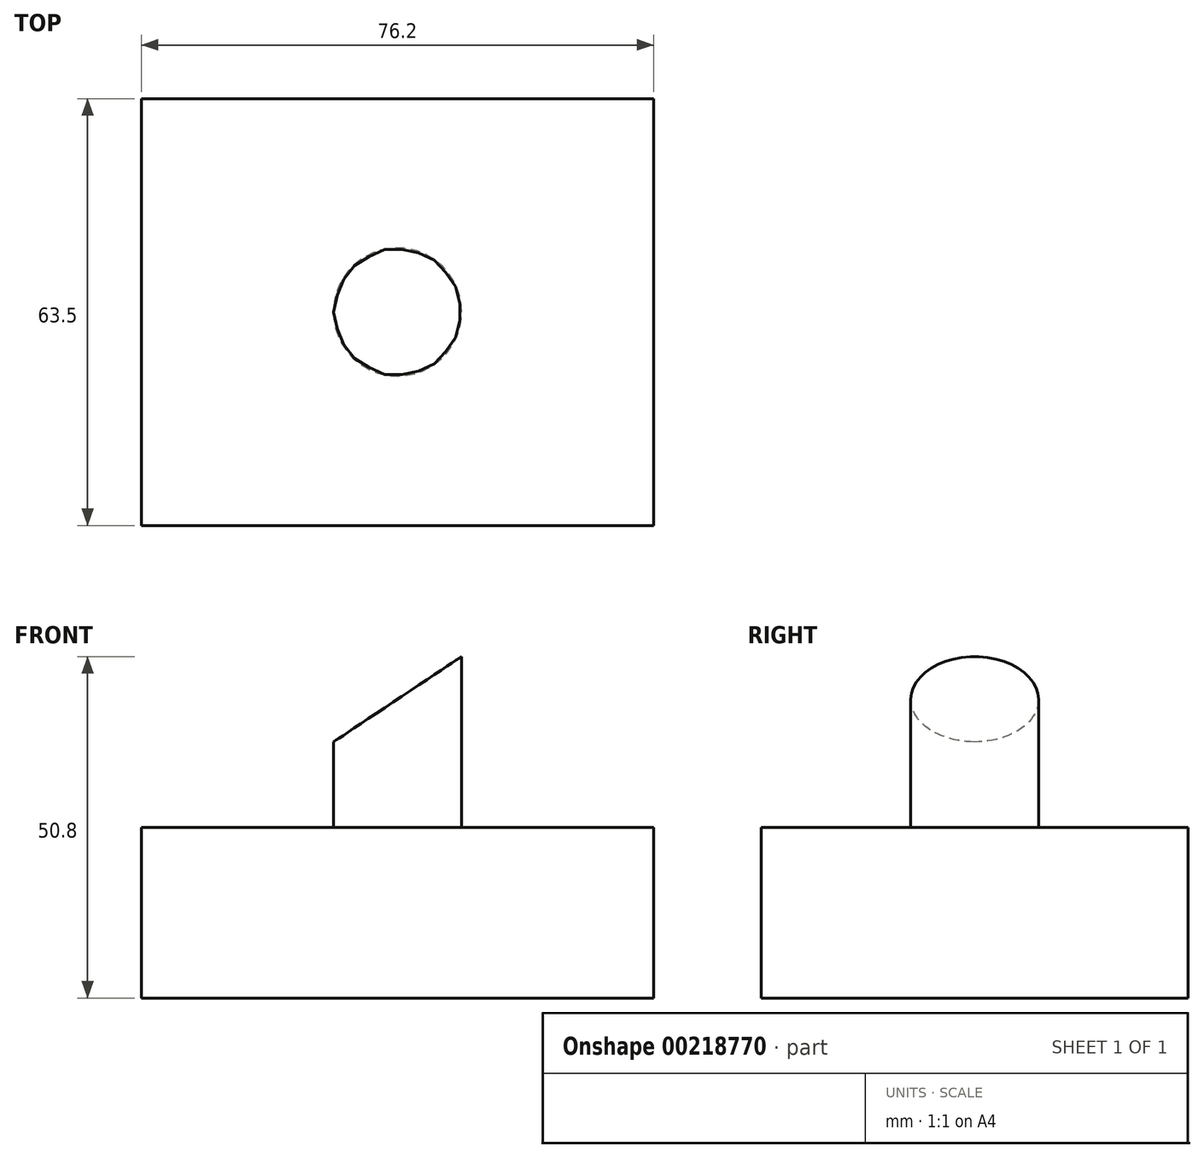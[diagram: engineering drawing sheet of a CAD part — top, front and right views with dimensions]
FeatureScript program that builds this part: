
annotation { "Feature Type Name" : "Feature", "Feature Type Description" : "" }
export const myFeature = defineFeature(function(context is Context, id is Id, definition is map)
    precondition{}
    {
        {
            var Q0;
            Q0=qCreatedBy(makeId("Top.planeOp"),FACE);
            var sketch = newSketch(context, id + "F0", { "sketchPlane" : qUnion([Q0])});
            skLineSegment(sketch, "E0.bottom", {"start": v(-38.1, 31.75) * mm, "end": v(38.1, 31.75) * mm});
            skLineSegment(sketch, "E0.top", {"start": v(-38.1, -31.75) * mm, "end": v(38.1, -31.75) * mm});
            skLineSegment(sketch, "E0.left", {"start": v(-38.1, 31.75) * mm, "end": v(-38.1, -31.75) * mm});
            skLineSegment(sketch, "E0.right", {"start": v(38.1, 31.75) * mm, "end": v(38.1, -31.75) * mm});
            skPoint(sketch, "E0.middle", {"position": v(0, 0) * mm});
            skSolve(sketch);
        }
        {
            var Q0;
            Q0 = qSketchRegion(id + "F0", true);
            extrude(context, id + "F1", {"entities" : qUnion([Q0]), "depth" : 25.4 * mm});
        }
        {
            var Q0;
            Q0=makeQuery(id+"F1.opExtrude","CAP_FACE",FACE,{"disambiguationData":[OSD([sQuery(id+"F0.wireOp",EDGE,"E0.bottom"),sQuery(id+"F0.wireOp",EDGE,"E0.top"),sQuery(id+"F0.wireOp",EDGE,"E0.left"),sQuery(id+"F0.wireOp",EDGE,"E0.right")])],"isStart":false});
            var sketch = newSketch(context, id + "F2", { "sketchPlane" : qUnion([Q0])});
            skCircle(sketch, "E1", {"center": v(0, 0) * mm, "radius": 9.53 * mm});
            skSolve(sketch);
        }
        {
            var Q0;
            Q0 = qSketchRegion(id + "F2", true);
            extrude(context, id + "F3", {"entities" : qUnion([Q0]), "operationType" : NewBodyOperationType.ADD, "depth" : 25.4 * mm});
        }
        {
            var Q0;
            Q0=qCreatedBy(makeId("Front.planeOp"),FACE);
            var sketch = newSketch(context, id + "F4", { "sketchPlane" : qUnion([Q0])});
            skLineSegment(sketch, "E2.0", {"start": v(-9.53, 50.8) * mm, "end": v(9.53, 50.8) * mm});
            skLineSegment(sketch, "E3", {"start": v(-9.53, 38.1) * mm, "end": v(-9.53, 50.8) * mm});
            skLineSegment(sketch, "E4", {"start": v(9.52, 50.8) * mm, "end": v(-9.53, 38.1) * mm});
            skPoint(sketch, "E5.orphan", {"position": v(-9.53, 25.4) * mm});
            skSolve(sketch);
        }
        {
            var Q0;
            Q0 = qSketchRegion(id + "F4", true);
            extrude(context, id + "F5", {"entities" : qUnion([Q0]), "operationType" : NewBodyOperationType.REMOVE, "endBound" : BoundingType.SYMMETRIC, "oppositeDirection" : true, "depth" : 38.1 * mm});
        }
    });
